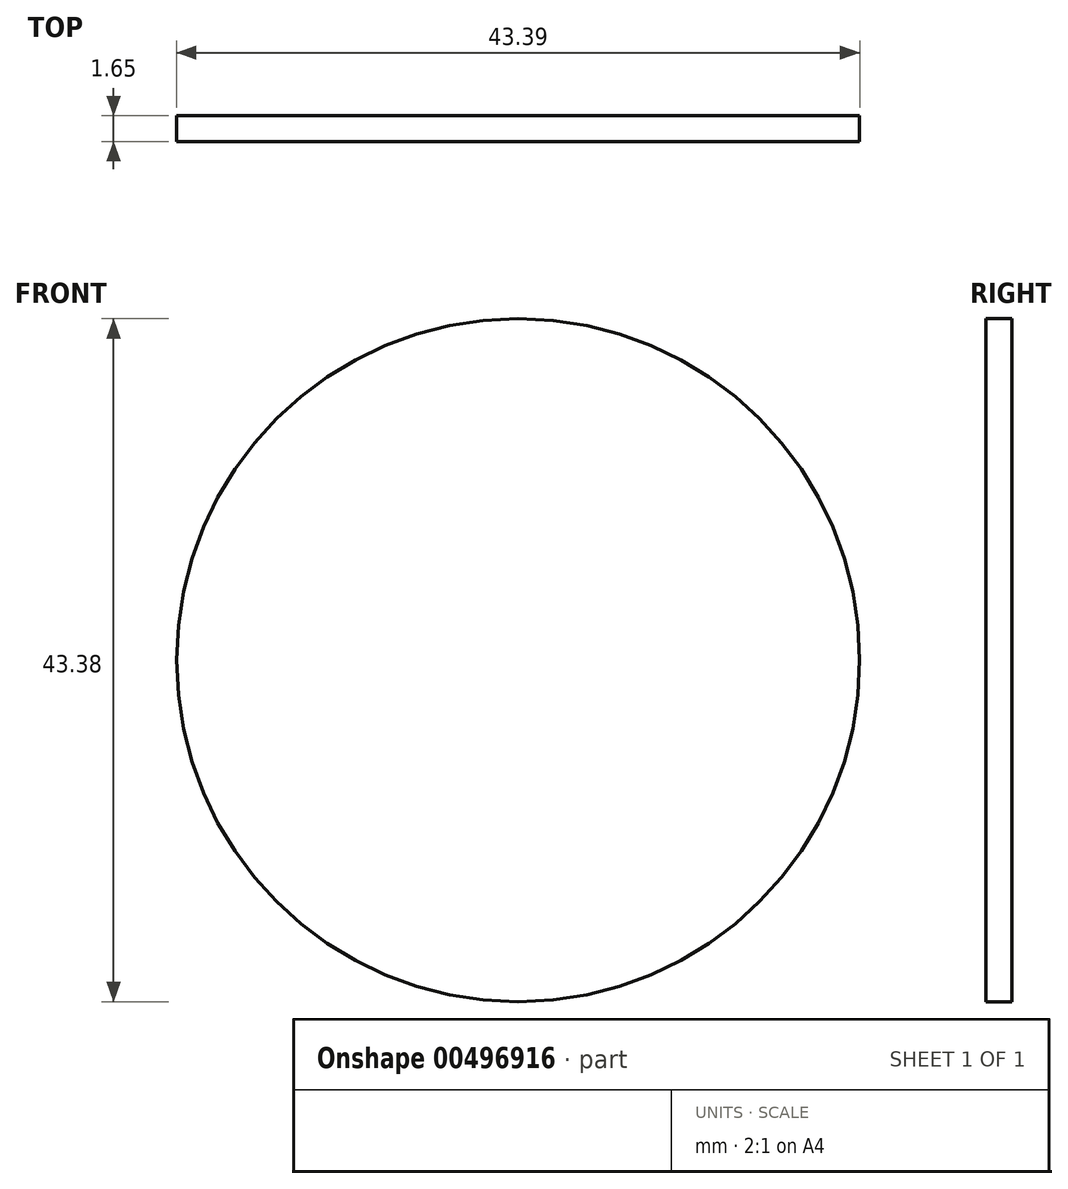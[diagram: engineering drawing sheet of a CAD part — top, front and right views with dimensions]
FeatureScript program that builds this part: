
annotation { "Feature Type Name" : "Feature", "Feature Type Description" : "" }
export const myFeature = defineFeature(function(context is Context, id is Id, definition is map)
    precondition{}
    {
        {
            var Q0;
            Q0=qCreatedBy(makeId("Front.planeOp"),FACE);
            var sketch = newSketch(context, id + "F0", { "sketchPlane" : qUnion([Q0])});
            skCircle(sketch, "E0", {"center": v(-61.89, 39.02) * mm, "radius": 21.7 * mm});
            skCircle(sketch, "E1", {"center": v(-46.2, -35.07) * mm, "radius": 21.7 * mm});
            skCircle(sketch, "E2", {"center": v(41.56, 38.35) * mm, "radius": 21.7 * mm});
            skCircle(sketch, "E3", {"center": v(36.9, -34.4) * mm, "radius": 21.7 * mm});
            skArc(sketch, "E4", {"start": v(-83.13, 34.62) * mm, "mid": v(-61.66, 33.15) * mm, "end": v(-40.37, 36.3) * mm});
            skArc(sketch, "E5", {"start": v(19.88, 37.7) * mm, "mid": v(41.45, 32.7) * mm, "end": v(63.2, 36.82) * mm});
            skArc(sketch, "E6", {"start": v(-67.85, -36.5) * mm, "mid": v(-46.06, -43.15) * mm, "end": v(-24.52, -35.73) * mm});
            skArc(sketch, "E7", {"start": v(15.2, -34.84) * mm, "mid": v(36.8, -41.6) * mm, "end": v(58.56, -35.4) * mm});
            skSolve(sketch);
        }
        {
            var Q0;
            {var subQ0=sQuery(id+"F0.wireOp",EDGE,"E4");Q0=makeQuery(id+"F0.imprint","IMPRINT",FACE,{"disambiguationData":[TD([[makeQuery(id+"F0.imprint","IMPRINT",EDGE,{"derivedFrom":subQ0}),1.0]])]});}
            var Q1;
            {var subQ0=sQuery(id+"F0.wireOp",EDGE,"E4");Q1=makeQuery(id+"F0.imprint","IMPRINT",FACE,{"disambiguationData":[TD([[makeQuery(id+"F0.imprint","IMPRINT",EDGE,{"derivedFrom":subQ0}),-1.0]])]});}
            extrude(context, id + "F1", {"entities" : qUnion([Q0, Q1]), "depth" : 1.65 * mm});
        }
    });
